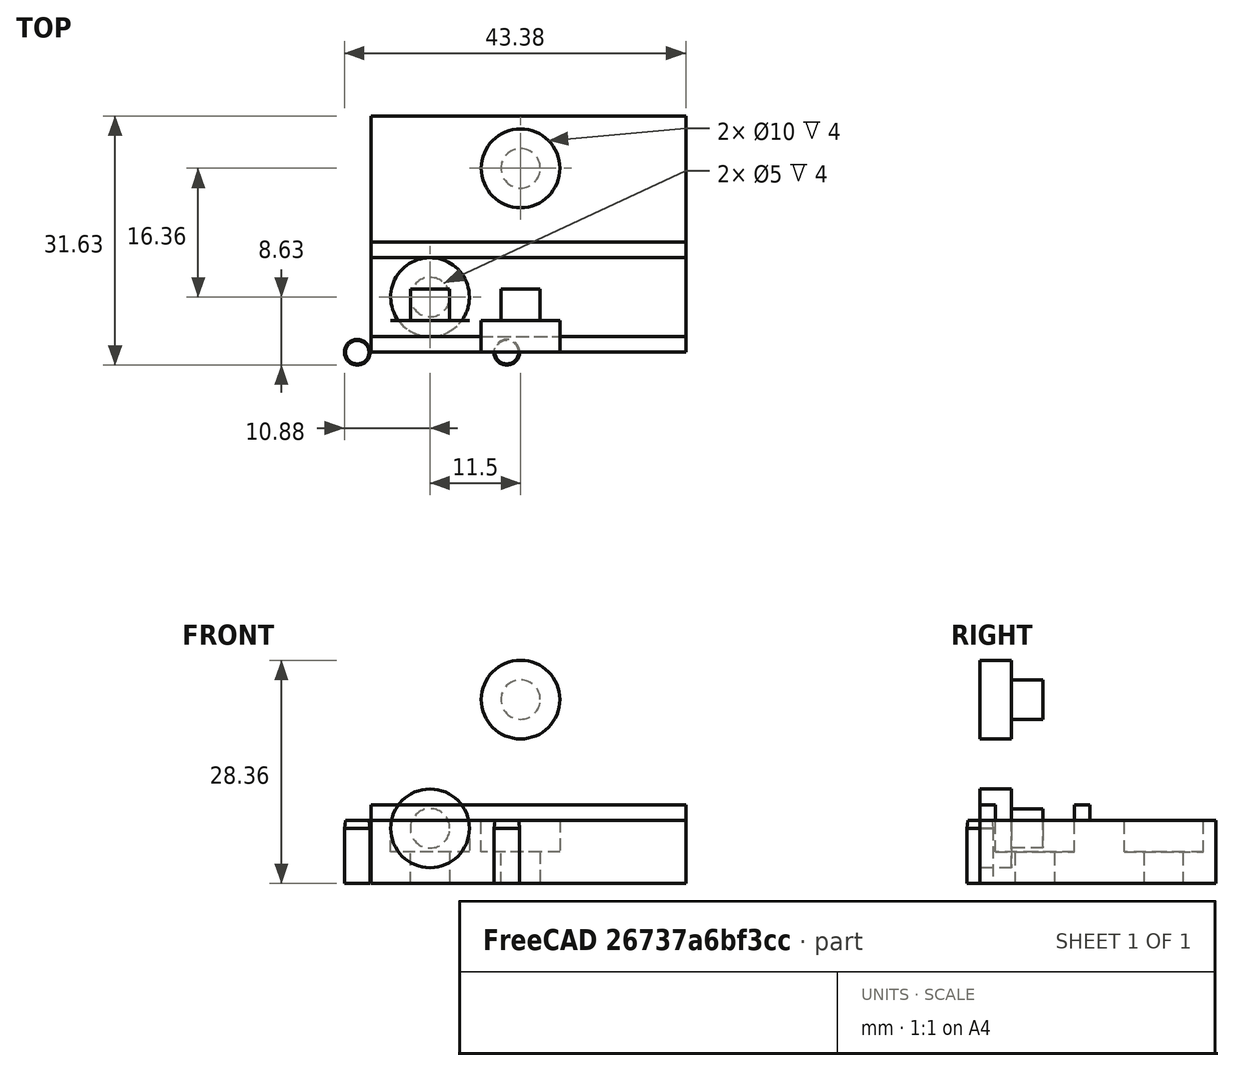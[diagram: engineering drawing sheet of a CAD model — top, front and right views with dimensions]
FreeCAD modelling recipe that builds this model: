
FCSTD DOCUMENT  (FreeCAD 0.20R29603 (Git))
Label: hacklab-fridge-door-sensor
License: CC BY-SA 4.0
LicenseURL: https://creativecommons.org/licenses/by-sa/4.0/
objects: Part::Cylinder×6, Part::Part2DObjectPython×4, Part::Box×3, App::Part×3, App::DocumentObjectGroup×2, PartDesign::AdditiveLoft×2, PartDesign::Body×2, Part::Cut×1
note: 20 computed .brp shape members not serialized (recipe doc carries the construction recipe); baked Part::Feature solids carry a one-line shape summary decoded from their .brp

FEATURE [Part::Box] Box  label="Block"
  AttacherType = Attacher::AttachEngine3D
  Height = 30
  Length = 40
  Width = 8
FEATURE [Part::Cylinder] Cylinder  label="Left screw hole (rear)"
  Angle = 360
  AttacherType = Attacher::AttachEngine3D
  FirstAngle = 0
  Height = 4
  Placement = pos=(7.5,4,7) rot=(-1,0,0;1.5708rad)
  Radius = 2.5
  SecondAngle = 0
FEATURE [Part::Cylinder] Cylinder001  label="Right screw hole (rear)"
  Angle = 360
  AttacherType = Attacher::AttachEngine3D
  FirstAngle = 0
  Height = 4
  Placement = pos=(19,4,23.36) rot=(-1,0,0;1.5708rad)
  Radius = 2.5
  SecondAngle = 0
FEATURE [Part::Cylinder] Cylinder002  label="Left screw hole (front)"
  Angle = 360
  AttacherType = Attacher::AttachEngine3D
  FirstAngle = 0
  Height = 4
  Placement = pos=(7.5,0,7) rot=(-1,0,0;1.5708rad)
  Radius = 5
  SecondAngle = 0
FEATURE [App::DocumentObjectGroup] Group  label="Left screw hole"
  Group = -> [Cylinder,Cylinder002]
FEATURE [Part::Cylinder] Cylinder003  label="Right screw hole (front)"
  Angle = 360
  AttacherType = Attacher::AttachEngine3D
  FirstAngle = 0
  Height = 4
  Placement = pos=(19,0,23.36) rot=(-1,0,0;1.5708rad)
  Radius = 5
  SecondAngle = 0
FEATURE [App::DocumentObjectGroup] Group001  label="Right screw hole"
  Group = -> [Cylinder001,Cylinder003]
FEATURE [App::Part] Part  label="Screw holes"
  Group = -> [Cylinder,Cylinder002,Group,Cylinder001,Cylinder003,Group001]
  Origin = -> Origin
FEATURE [Part::Cut] Cut  label="Cut screw holes"
  Base = -> Box
  Placement = pos=(0,0,8) rot=(-1,0,0;1.5708rad)
  Tool = -> Part
FEATURE [Part::Cylinder] Cylinder004  label="Left post"
  Angle = 360
  AttacherType = Attacher::AttachEngine3D
  FirstAngle = 0
  Height = 7
  Placement = pos=(-1.75,0,0) rot=(0,0,1;0rad)
  Radius = 1.63
  SecondAngle = 0
FEATURE [Part::Cylinder] Cylinder005  label="Right post"
  Angle = 360
  AttacherType = Attacher::AttachEngine3D
  FirstAngle = 0
  Height = 7
  Placement = pos=(17.25,0,0) rot=(0,0,1;0rad)
  Radius = 1.63
  SecondAngle = 0
FEATURE [Part::Part2DObjectPython] Circle  label="Left post (rear)"  # Draft 2D object (typed FeaturePython)
  Area = 8.3469
  FirstAngle = 0
  LastAngle = 0
  MakeFace = true
  Placement = pos=(0,0,7) rot=(0,0,1;0rad)
  Radius = 1.63
FEATURE [Part::Part2DObjectPython] Circle001  label="Right post (rear)"  # Draft 2D object (typed FeaturePython)
  Area = 8.3469
  FirstAngle = 0
  LastAngle = 0
  MakeFace = true
  Placement = pos=(19,0,7) rot=(0,0,1;0rad)
  Radius = 1.63
FEATURE [Part::Part2DObjectPython] Circle002  label="Left post (front)"  # Draft 2D object (typed FeaturePython)
  Area = 7.06858
  FirstAngle = 0
  LastAngle = 0
  MakeFace = true
  Placement = pos=(0,0,8) rot=(0,0,1;0rad)
  Radius = 1.5
FEATURE [Part::Part2DObjectPython] Circle003  label="Right post (front)"  # Draft 2D object (typed FeaturePython)
  Area = 7.06858
  FirstAngle = 0
  LastAngle = 0
  MakeFace = true
  Placement = pos=(19,0,8) rot=(0,0,1;0rad)
  Radius = 1.5
FEATURE [PartDesign::AdditiveLoft] AdditiveLoft  label="Left post (loft)"
  Closed = false
  Placement = pos=(0,0,8) rot=(0,0,1;0rad)
  Profile = -> Circle002
  Ruled = false
  Sections = -> [Circle]
FEATURE [PartDesign::Body] Body  label="Left post (body)"
  Group = -> [Circle002,Circle,AdditiveLoft]
  Origin = -> Origin002
  Placement = pos=(-1.75,0,0) rot=(0,0,1;0rad)
  Tip = -> AdditiveLoft
FEATURE [PartDesign::AdditiveLoft] AdditiveLoft001  label="Right post (loft)"
  Closed = false
  Placement = pos=(19,0,8) rot=(0,0,1;0rad)
  Profile = -> Circle003
  Ruled = false
  Sections = -> [Circle001]
FEATURE [PartDesign::Body] Body001  label="Right post (body)"
  Group = -> [Circle003,Circle001,AdditiveLoft001]
  Origin = -> Origin003
  Placement = pos=(-1.75,0,0) rot=(0,0,1;0rad)
  Tip = -> AdditiveLoft001
FEATURE [App::Part] Part001  label="Posts"
  Group = -> [Cylinder004,Cylinder005,Body,Body001]
  Origin = -> Origin001
  Placement = pos=(-16,-7,8) rot=(0,0,1;3.14159rad)
FEATURE [Part::Box] Box001  label="Guard (top)"
  AttacherType = Attacher::AttachEngine3D
  Height = 2
  Length = 40
  Placement = pos=(0,12,8) rot=(0,0,1;0rad)
  Width = 2
FEATURE [Part::Box] Box002  label="Guard (bottom)"
  AttacherType = Attacher::AttachEngine3D
  Height = 2
  Length = 40
  Placement = pos=(0,0,8) rot=(0,0,1;0rad)
  Width = 2
FEATURE [App::Part] Part002  label="Main"
  Group = -> [Box,Part,Cut,Box001,Box002]
  Origin = -> Origin005
  Placement = pos=(0,0,0) rot=(0,0,1;3.14159rad)
